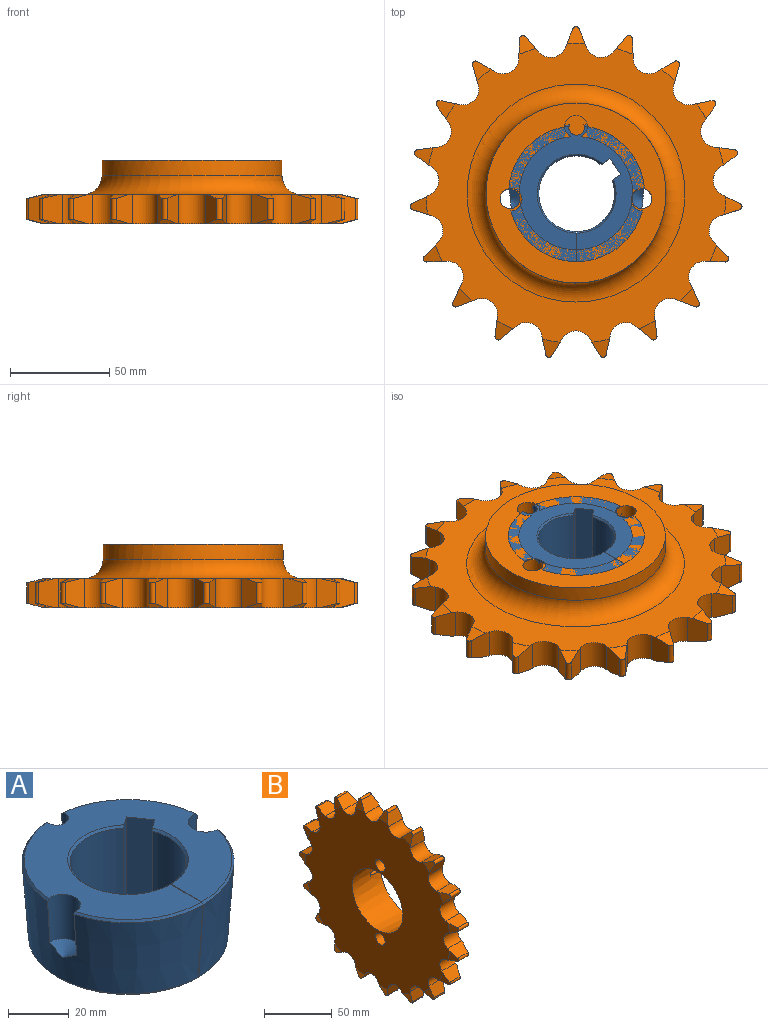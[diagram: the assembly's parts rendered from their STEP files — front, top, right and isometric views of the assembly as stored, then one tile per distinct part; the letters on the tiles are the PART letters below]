
ASSEMBLY  parts=2 mates=1
PART A: 26 faces, bbox 73.8x69.5x31.8 mm
  f0: cylinder r=3.94mm len=31.75mm, axis (0,0,1), area 408.2mm2, adj f5,f6,f10,f11,f14,f15,f16,f17
  f1: cylinder r=5.75mm len=17.86mm, axis (0,0,1), area 339.7mm2, adj f2,f10,f13,f14,f16
  f2: cone r=5.75mm half-angle=59deg, axis (0,0,1), area 61.3mm2, adj f1,f10
  f3: cone r=5.75mm half-angle=59deg, axis (0,0,1), area 61.4mm2, adj f6,f23
  f4: cone r=19.05mm half-angle=45deg, axis (0,0,1), area 42.1mm2, adj f7,f14,f21,f24
  f5: cone r=32.76mm half-angle=45deg, axis (0,0,1), area 118mm2, adj f0,f6,f17,f24
  f6: cone r=32.7mm half-angle=4deg, axis (0,0,1), area 2870.6mm2, adj f0,f3,f5,f15,f19,f23,f24
  f7: cylinder r=19.05mm len=30.16mm, axis (0,0,1), area 1105.3mm2, adj f4,f18,f21,f24
  f8: cone r=19.84mm half-angle=45deg, axis (0,0,-1), area 84mm2, adj f9,f17,f22,f25
  f9: cylinder r=19.05mm len=38.1mm, axis (0,0,1), area 2208.5mm2, adj f8,f12,f22,f25
  f10: cone r=32.7mm half-angle=4deg, axis (0,0,1), area 2870.7mm2, adj f0,f1,f2,f11,f13,f16,f25
  f11: cone r=32.76mm half-angle=45deg, axis (0,0,1), area 118mm2, adj f0,f10,f17,f25
  f12: cone r=19.05mm half-angle=45deg, axis (0,0,1), area 84mm2, adj f9,f14,f22,f25
  f13: cone r=34.18mm half-angle=41deg, axis (0,0,-1), area 47.6mm2, adj f1,f10,f14,f25
  f14: plane 68.14x68.14mm, normal (0,0,1), area 2240.8mm2, adj f0,f1,f4,f12,f13,f15,f16,f19
  f15: cone r=34.18mm half-angle=41deg, axis (0,0,-1), area 50.1mm2, adj f0,f6,f14,f23
  f16: cone r=34.18mm half-angle=41deg, axis (0,0,-1), area 50.1mm2, adj f0,f1,f10,f14
  f17: plane 63.82x63.62mm, normal (0,0,-1), area 1907.1mm2, adj f0,f5,f8,f11,f18,f20,f21,f22
  f18: cone r=19.84mm half-angle=45deg, axis (0,0,-1), area 42.1mm2, adj f7,f17,f21,f24
  f19: cone r=34.18mm half-angle=41deg, axis (0,0,-1), area 47.6mm2, adj f6,f14,f23,f24
  f20: plane 31.75x7.8mm, normal (-0.82,-0.57,0), area 302.4mm2, adj f14,f17,f21,f22
  f21: plane 31.75x4.4mm, normal (-0.57,0.82,0), area 169.8mm2, adj f4,f7,f14,f17,f18,f20
  f22: plane 31.75x4.4mm, normal (0.57,-0.82,0), area 169.8mm2, adj f8,f9,f12,f14,f17,f20
  f23: cylinder r=5.75mm len=17.86mm, axis (0,0,1), area 339.7mm2, adj f3,f6,f14,f15,f19
  f24: plane 31.75x15.82mm, normal (-1,0,0), area 467.5mm2, adj f4,f5,f6,f7,f14,f17,f18,f19
  f25: plane 31.75x15.82mm, normal (1,0,0), area 467.5mm2, adj f8,f9,f10,f11,f12,f13,f14,f17
PART B: 124 faces, bbox 31.9x166.5x167.3 mm
  f0: cylinder r=5.75mm len=11.51mm, axis (1,0,0), area 370.6mm2, adj f3,f21,f123
  f1: cylinder r=4.96mm len=31.75mm, axis (1,0,0), area 987.6mm2, adj f3,f20,f21
  f2: cylinder r=4.96mm len=31.75mm, axis (1,0,0), area 987.6mm2, adj f3,f20,f21
  f3: cone r=28.49mm half-angle=4deg, axis (1,0,0), area 5426.7mm2, adj f0,f1,f2,f20,f21,f123
  f4: torus R=54.77mm, axis (-1,0,0), area 4578.7mm2, adj f6,f85
  f5: cone r=75.39mm half-angle=75deg, axis (1,0,0), area 48.2mm2, adj f20,f25,f26,f82
  f6: cylinder r=45.24mm len=90.49mm, axis (1,0,0), area 2166.2mm2, adj f4,f21
  f7: cylinder r=7.94mm len=14.61mm, axis (-1,0,0), area 238.2mm2, adj f20,f76,f77,f85
  f8: cylinder r=7.94mm len=14.61mm, axis (-1,0,0), area 238.2mm2, adj f20,f73,f74,f85
  f9: cylinder r=7.94mm len=14.61mm, axis (-1,0,0), area 238.2mm2, adj f20,f70,f71,f85
  f10: cylinder r=7.94mm len=14.61mm, axis (-1,0,0), area 238.2mm2, adj f20,f67,f68,f85
  f11: cylinder r=7.94mm len=14.61mm, axis (-1,0,0), area 238.2mm2, adj f20,f64,f65,f85
  f12: cylinder r=7.94mm len=14.61mm, axis (-1,0,0), area 238.2mm2, adj f20,f61,f62,f85
  f13: cylinder r=1.66mm len=10.69mm, axis (-1,0,0), area 41mm2, adj f45,f51,f96,f105
  f14: cylinder r=1.66mm len=10.69mm, axis (-1,0,0), area 41.7mm2, adj f42,f47,f97,f106
  f15: cylinder r=1.66mm len=10.69mm, axis (-1,0,0), area 41.4mm2, adj f39,f44,f98,f107
  f16: cylinder r=1.66mm len=10.69mm, axis (-1,0,0), area 41.3mm2, adj f36,f41,f99,f108
  f17: cylinder r=1.66mm len=10.69mm, axis (-1,0,0), area 41.3mm2, adj f33,f38,f100,f109
  f18: cylinder r=1.66mm len=10.69mm, axis (-1,0,0), area 41.6mm2, adj f30,f35,f101,f110
  f19: cylinder r=1.66mm len=10.69mm, axis (-1,0,0), area 42mm2, adj f27,f32,f102,f111
  f20: plane 150.73x150.35mm, normal (-1,0,0), area 14211.7mm2, adj f1,f2,f3,f5,f7,f8,f9,f10
  f21: plane 90.49x90.49mm, normal (1,0,0), area 3626.7mm2, adj f0,f1,f2,f3,f6
  f22: cylinder r=1.66mm len=10.69mm, axis (-1,0,0), area 42.4mm2, adj f23,f29,f103,f112
  f23: plane 14.76x7.92mm, normal (0,0.65,-0.76), area 133.8mm2, adj f20,f22,f24,f85,f103,f112
  f24: cylinder r=7.94mm len=14.61mm, axis (-1,0,0), area 238.2mm2, adj f20,f23,f25,f85
  f25: plane 14.76x9.66mm, normal (0,0.37,0.93), area 133.8mm2, adj f5,f20,f24,f26,f85,f113
  f26: cylinder r=1.66mm len=10.69mm, axis (-1,0,0), area 41.8mm2, adj f5,f25,f82,f113
  f27: plane 14.76x8.98mm, normal (0,0.86,-0.51), area 133.8mm2, adj f19,f20,f28,f85,f102,f111
  f28: cylinder r=7.94mm len=14.61mm, axis (-1,0,0), area 238.2mm2, adj f20,f27,f29,f85
  f29: plane 14.76x10.37mm, normal (0,0.05,1), area 133.8mm2, adj f20,f22,f28,f85,f103,f112
  f30: plane 14.76x10.18mm, normal (0,0.98,-0.2), area 133.8mm2, adj f18,f20,f31,f85,f101,f110
  f31: cylinder r=7.94mm len=14.61mm, axis (-1,0,0), area 238.2mm2, adj f20,f30,f32,f85
  f32: plane 14.76x9.98mm, normal (0,-0.28,0.96), area 133.8mm2, adj f19,f20,f31,f85,f102,f111
  f33: plane 14.76x10.3mm, normal (0,0.99,0.13), area 133.8mm2, adj f17,f20,f34,f85,f100,f109
  f34: cylinder r=7.94mm len=14.61mm, axis (-1,0,0), area 238.2mm2, adj f20,f33,f35,f85
  f35: plane 14.76x8.52mm, normal (0,-0.58,0.82), area 133.8mm2, adj f18,f20,f34,f85,f101,f110
  f36: plane 14.76x9.32mm, normal (0,0.9,0.44), area 133.8mm2, adj f16,f20,f37,f85,f99,f108
  f37: cylinder r=7.94mm len=14.61mm, axis (-1,0,0), area 238.2mm2, adj f20,f36,f38,f85
  f38: plane 14.76x8.44mm, normal (0,-0.81,0.59), area 133.8mm2, adj f17,f20,f37,f85,f100,f109
  f39: plane 14.76x7.43mm, normal (0,0.7,0.71), area 133.8mm2, adj f15,f20,f40,f85,f98,f107
  f40: cylinder r=7.94mm len=14.61mm, axis (-1,0,0), area 238.2mm2, adj f20,f39,f41,f85
  f41: plane 14.76x9.94mm, normal (0,-0.96,0.29), area 133.8mm2, adj f16,f20,f40,f85,f99,f108
  f42: plane 14.76x9.37mm, normal (0,0.43,0.9), area 133.8mm2, adj f14,f20,f43,f85,f97,f106
  f43: cylinder r=7.94mm len=14.61mm, axis (-1,0,0), area 238.2mm2, adj f20,f42,f44,f85
  f44: plane 14.76x10.38mm, normal (0,-1,-0.04), area 133.8mm2, adj f15,f20,f43,f85,f98,f107
  f45: plane 14.76x10.31mm, normal (0,0.12,0.99), area 133.8mm2, adj f13,f20,f46,f85,f96,f105
  f46: cylinder r=7.94mm len=14.61mm, axis (-1,0,0), area 238.2mm2, adj f20,f45,f47,f85
  f47: plane 14.76x9.71mm, normal (0,-0.93,-0.36), area 133.8mm2, adj f14,f20,f46,f85,f97,f106
  f48: cylinder r=1.66mm len=10.69mm, axis (-1,0,0), area 42.4mm2, adj f49,f55,f95,f104
  f49: plane 14.76x10.15mm, normal (0,-0.21,0.98), area 133.8mm2, adj f20,f48,f50,f85,f95,f104
  f50: cylinder r=7.94mm len=14.61mm, axis (-1,0,0), area 238.2mm2, adj f20,f49,f51,f85
  f51: plane 14.76x8mm, normal (0,-0.77,-0.64), area 133.8mm2, adj f13,f20,f50,f85,f96,f105
  f52: cylinder r=1.66mm len=10.69mm, axis (-1,0,0), area 42.4mm2, adj f53,f59,f94,f122
  f53: plane 14.76x8.91mm, normal (0,-0.52,0.86), area 133.8mm2, adj f20,f52,f54,f85,f94,f122
  f54: cylinder r=7.94mm len=14.61mm, axis (-1,0,0), area 238.2mm2, adj f20,f53,f55,f85
  f55: plane 14.76x8.91mm, normal (0,-0.52,-0.86), area 133.8mm2, adj f20,f48,f54,f85,f95,f104
  f56: cylinder r=1.66mm len=10.69mm, axis (-1,0,0), area 42.4mm2, adj f57,f62,f93,f121
  f57: plane 14.76x8mm, normal (0,-0.77,0.64), area 133.8mm2, adj f20,f56,f58,f85,f93,f121
  f58: cylinder r=7.94mm len=14.61mm, axis (-1,0,0), area 238.2mm2, adj f20,f57,f59,f85
  f59: plane 14.76x10.15mm, normal (0,-0.21,-0.98), area 133.8mm2, adj f20,f52,f58,f85,f94,f122
  f60: cylinder r=1.66mm len=10.69mm, axis (-1,0,0), area 42.4mm2, adj f61,f65,f92,f120
  f61: plane 14.76x9.71mm, normal (0,-0.93,0.36), area 133.8mm2, adj f12,f20,f60,f85,f92,f120
  f62: plane 14.76x10.31mm, normal (0,0.12,-0.99), area 133.8mm2, adj f12,f20,f56,f85,f93,f121
  f63: cylinder r=1.66mm len=10.69mm, axis (-1,0,0), area 42.4mm2, adj f64,f68,f91,f119
  f64: plane 14.76x10.38mm, normal (0,-1,0.04), area 133.8mm2, adj f11,f20,f63,f85,f91,f119
  f65: plane 14.76x9.37mm, normal (0,0.43,-0.9), area 133.8mm2, adj f11,f20,f60,f85,f92,f120
  f66: cylinder r=1.66mm len=10.69mm, axis (-1,0,0), area 42.4mm2, adj f67,f71,f90,f118
  f67: plane 14.76x9.94mm, normal (0,-0.96,-0.29), area 133.8mm2, adj f10,f20,f66,f85,f90,f118
  f68: plane 14.76x7.43mm, normal (0,0.7,-0.71), area 133.8mm2, adj f10,f20,f63,f85,f91,f119
  f69: cylinder r=1.66mm len=10.69mm, axis (-1,0,0), area 42.4mm2, adj f70,f74,f89,f117
  f70: plane 14.76x8.44mm, normal (0,-0.81,-0.59), area 133.8mm2, adj f9,f20,f69,f85,f89,f117
  f71: plane 14.76x9.32mm, normal (0,0.9,-0.44), area 133.8mm2, adj f9,f20,f66,f85,f90,f118
  f72: cylinder r=1.66mm len=10.69mm, axis (-1,0,0), area 42.4mm2, adj f73,f77,f88,f116
  f73: plane 14.76x8.52mm, normal (0,-0.58,-0.82), area 133.8mm2, adj f8,f20,f72,f85,f88,f116
  f74: plane 14.76x10.3mm, normal (0,0.99,-0.13), area 133.8mm2, adj f8,f20,f69,f85,f89,f117
  f75: cylinder r=1.66mm len=10.69mm, axis (-1,0,0), area 42.4mm2, adj f76,f81,f87,f115
  f76: plane 14.76x9.98mm, normal (0,-0.28,-0.96), area 133.8mm2, adj f7,f20,f75,f85,f87,f115
  f77: plane 14.76x10.18mm, normal (0,0.98,0.2), area 133.8mm2, adj f7,f20,f72,f85,f88,f116
  f78: cylinder r=1.66mm len=10.69mm, axis (-1,0,0), area 42.4mm2, adj f79,f84,f86,f114
  f79: plane 14.76x10.37mm, normal (0,0.05,-1), area 133.8mm2, adj f20,f78,f80,f85,f86,f114
  f80: cylinder r=7.94mm len=14.61mm, axis (-1,0,0), area 238.2mm2, adj f20,f79,f81,f85
  f81: plane 14.76x8.98mm, normal (0,0.86,0.51), area 133.8mm2, adj f20,f75,f80,f85,f87,f115
  f82: plane 14.76x9.66mm, normal (0,0.37,-0.93), area 133.8mm2, adj f5,f20,f26,f83,f85,f113
  f83: cylinder r=7.94mm len=14.61mm, axis (-1,0,0), area 238.2mm2, adj f20,f82,f84,f85
  f84: plane 14.76x7.92mm, normal (0,0.65,0.76), area 133.8mm2, adj f20,f78,f83,f85,f86,f114
  f85: plane 150.73x150.35mm, normal (1,0,0), area 7110.1mm2, adj f4,f7,f8,f9,f10,f11,f12,f23
  f86: cone r=75.39mm half-angle=75deg, axis (1,0,0), area 46.5mm2, adj f20,f78,f79,f84
  f87: cone r=75.39mm half-angle=75deg, axis (1,0,0), area 46.5mm2, adj f20,f75,f76,f81
  f88: cone r=75.39mm half-angle=75deg, axis (1,0,0), area 46.5mm2, adj f20,f72,f73,f77
  f89: cone r=75.39mm half-angle=75deg, axis (1,0,0), area 46.5mm2, adj f20,f69,f70,f74
  f90: cone r=75.39mm half-angle=75deg, axis (1,0,0), area 46.5mm2, adj f20,f66,f67,f71
  f91: cone r=75.39mm half-angle=75deg, axis (1,0,0), area 46.5mm2, adj f20,f63,f64,f68
  f92: cone r=75.39mm half-angle=75deg, axis (1,0,0), area 46.5mm2, adj f20,f60,f61,f65
  f93: cone r=75.39mm half-angle=75deg, axis (1,0,0), area 46.5mm2, adj f20,f56,f57,f62
  f94: cone r=75.39mm half-angle=75deg, axis (1,0,0), area 46.5mm2, adj f20,f52,f53,f59
  f95: cone r=75.39mm half-angle=75deg, axis (1,0,0), area 46.5mm2, adj f20,f48,f49,f55
  f96: cone r=75.39mm half-angle=75deg, axis (1,0,0), area 48.9mm2, adj f13,f20,f45,f51
  f97: cone r=75.39mm half-angle=75deg, axis (1,0,0), area 48.9mm2, adj f14,f20,f42,f47
  f98: cone r=75.39mm half-angle=75deg, axis (1,0,0), area 48mm2, adj f15,f20,f39,f44
  f99: cone r=75.39mm half-angle=75deg, axis (1,0,0), area 48.2mm2, adj f16,f20,f36,f41
  f100: cone r=75.39mm half-angle=75deg, axis (1,0,0), area 48.1mm2, adj f17,f20,f33,f38
  f101: cone r=75.39mm half-angle=75deg, axis (1,0,0), area 48.9mm2, adj f18,f20,f30,f35
  f102: cone r=75.39mm half-angle=75deg, axis (1,0,0), area 48.9mm2, adj f19,f20,f27,f32
  f103: cone r=75.39mm half-angle=75deg, axis (1,0,0), area 46.5mm2, adj f20,f22,f23,f29
  f104: cone r=83.73mm half-angle=75deg, axis (-1,0,0), area 46.5mm2, adj f48,f49,f55,f85
  f105: cone r=83.73mm half-angle=75deg, axis (-1,0,0), area 48.9mm2, adj f13,f45,f51,f85
  f106: cone r=83.73mm half-angle=75deg, axis (-1,0,0), area 48.9mm2, adj f14,f42,f47,f85
  f107: cone r=83.73mm half-angle=75deg, axis (-1,0,0), area 48mm2, adj f15,f39,f44,f85
  f108: cone r=83.73mm half-angle=75deg, axis (-1,0,0), area 48.2mm2, adj f16,f36,f41,f85
  f109: cone r=83.73mm half-angle=75deg, axis (-1,0,0), area 48.1mm2, adj f17,f33,f38,f85
  f110: cone r=83.73mm half-angle=75deg, axis (-1,0,0), area 48.9mm2, adj f18,f30,f35,f85
  f111: cone r=83.73mm half-angle=75deg, axis (-1,0,0), area 48.9mm2, adj f19,f27,f32,f85
  f112: cone r=83.73mm half-angle=75deg, axis (-1,0,0), area 46.5mm2, adj f22,f23,f29,f85
  f113: cone r=83.73mm half-angle=75deg, axis (-1,0,0), area 46.5mm2, adj f25,f26,f82,f85
  f114: cone r=83.73mm half-angle=75deg, axis (-1,0,0), area 46.5mm2, adj f78,f79,f84,f85
  f115: cone r=83.73mm half-angle=75deg, axis (-1,0,0), area 46.5mm2, adj f75,f76,f81,f85
  f116: cone r=83.73mm half-angle=75deg, axis (-1,0,0), area 46.5mm2, adj f72,f73,f77,f85
  f117: cone r=83.73mm half-angle=75deg, axis (-1,0,0), area 46.5mm2, adj f69,f70,f74,f85
  f118: cone r=83.73mm half-angle=75deg, axis (-1,0,0), area 46.5mm2, adj f66,f67,f71,f85
  f119: cone r=83.73mm half-angle=75deg, axis (-1,0,0), area 46.5mm2, adj f63,f64,f68,f85
  f120: cone r=83.73mm half-angle=75deg, axis (-1,0,0), area 46.5mm2, adj f60,f61,f65,f85
  f121: cone r=83.73mm half-angle=75deg, axis (-1,0,0), area 46.5mm2, adj f56,f57,f62,f85
  f122: cone r=83.73mm half-angle=75deg, axis (-1,0,0), area 46.5mm2, adj f52,f53,f59,f85
  f123: plane 11.51x11.43mm, normal (1,0,0), area 103.9mm2, adj f0,f3
PLACE A t=(19.99,12.03,0.6)mm
PLACE B rot(axis=(0,-1,0),90deg) t=(19.67,12.36,-15.28)mm
MATE fastened B.f21 <-> A.f14  axis (0,0,1) through (19.67,11.56,16.47)mm
